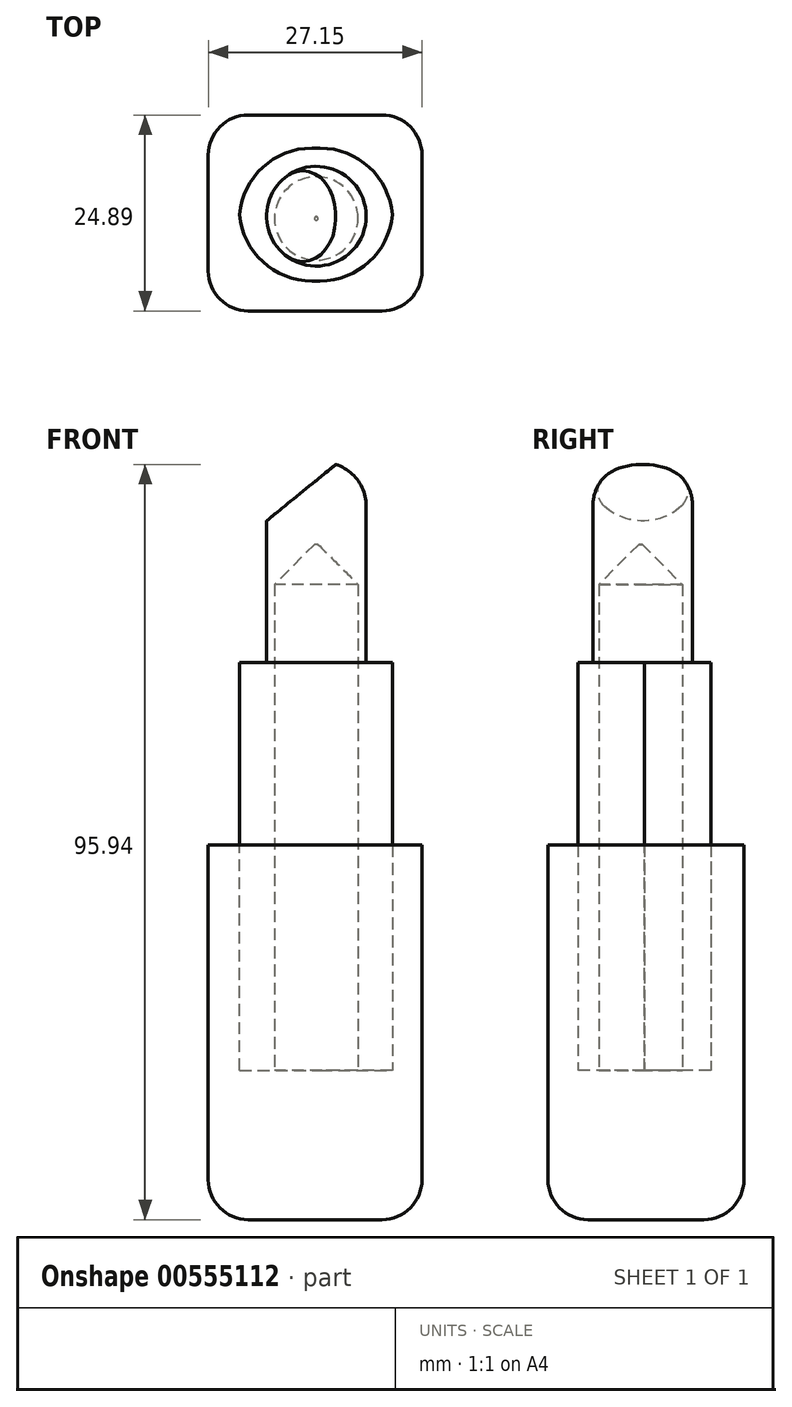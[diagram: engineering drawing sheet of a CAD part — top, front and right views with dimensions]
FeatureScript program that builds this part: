
annotation { "Feature Type Name" : "Feature", "Feature Type Description" : "" }
export const myFeature = defineFeature(function(context is Context, id is Id, definition is map)
    precondition{}
    {
        {
            var Q0;
            Q0=qCreatedBy(makeId("Front.planeOp"),FACE);
            var sketch = newSketch(context, id + "F0", { "sketchPlane" : qUnion([Q0])});
            skCircle(sketch, "E0", {"center": v(0, 0) * mm, "radius": 46.22 * mm});
            skSolve(sketch);
        }
        {
            var Q0;
            Q0=makeQuery(id+"F0.imprint","IMPRINT",FACE,{"disambiguationData":[TD([[makeQuery(id+"F0.imprint","IMPRINT",EDGE,{"derivedFrom":sQuery(id+"F0.wireOp",EDGE,"E0")}),1.0]])]});
            extrude(context, id + "F1", {"entities" : qUnion([Q0]), "depth" : 68.83 * mm, "offsetDistance" : 25.4 * mm});
        }
        {
            var Q0;
            Q0=makeQuery(id+"F1.opExtrude","SWEPT_FACE",FACE,{"disambiguationData":[OSD([sQuery(id+"F0.wireOp",EDGE,"E0")])]});
            fillet(context, id + "F2", {"entities" : qUnion([Q0]), "radius" : 33.73 * mm, "tangentPropagation" : true, "allowEdgeOverflow" : false});
        }
        {
            var Q0;
            Q0=makeQuery(id+"F1.opExtrude","SWEPT_BODY",BODY,{"disambiguationData":[OSD([sQuery(id+"F0.wireOp",EDGE,"E0")])]});
            deleteBodies(context, id + "F3", {"entities" : qUnion([Q0])});
        }
        {
            var Q0;
            Q0=qCreatedBy(makeId("Front.planeOp"),FACE);
            var sketch = newSketch(context, id + "F4", { "sketchPlane" : qUnion([Q0])});
            skLineSegment(sketch, "E1.bottom", {"start": v(-13.72, -18.98) * mm, "end": v(13.43, -18.98) * mm});
            skLineSegment(sketch, "E1.top", {"start": v(-13.72, 28.62) * mm, "end": v(13.43, 28.62) * mm});
            skLineSegment(sketch, "E1.left", {"start": v(-13.72, -18.98) * mm, "end": v(-13.72, 28.62) * mm});
            skLineSegment(sketch, "E1.right", {"start": v(13.43, -18.98) * mm, "end": v(13.43, 28.62) * mm});
            skSolve(sketch);
        }
        {
            var Q0;
            Q0=makeQuery(id+"F4.imprint","IMPRINT",FACE,{"disambiguationData":[TD([[makeQuery(id+"F4.imprint","IMPRINT",EDGE,{"derivedFrom":sQuery(id+"F4.wireOp",EDGE,"E1.bottom")}),1.0]])]});
            extrude(context, id + "F5", {"entities" : qUnion([Q0]), "depth" : 24.9 * mm, "offsetDistance" : 25.4 * mm});
        }
        {
            var Q0;
            Q0=makeQuery(id+"F5.opExtrude","CAP_EDGE",EDGE,{"disambiguationData":[OSD([sQuery(id+"F4.wireOp",EDGE,"E1.right")])],"isStart":false});
            var Q1;
            Q1=makeQuery(id+"F5.opExtrude","CAP_EDGE",EDGE,{"disambiguationData":[OSD([sQuery(id+"F4.wireOp",EDGE,"E1.right")])],"isStart":true});
            var Q2;
            Q2=makeQuery(id+"F5.opExtrude","CAP_EDGE",EDGE,{"disambiguationData":[OSD([sQuery(id+"F4.wireOp",EDGE,"E1.left")])],"isStart":true});
            var Q3;
            Q3=makeQuery(id+"F5.opExtrude","CAP_EDGE",EDGE,{"disambiguationData":[OSD([sQuery(id+"F4.wireOp",EDGE,"E1.left")])],"isStart":false});
            fillet(context, id + "F6", {"entities" : qUnion([Q0, Q1, Q2, Q3]), "radius" : 5.08 * mm, "tangentPropagation" : true, "allowEdgeOverflow" : false});
        }
        {
            var Q0;
            Q0=makeQuery(id+"F6.opFillet","BLEND_EDGE",EDGE,{"blendedFrom":[makeQuery(id+"F5.opExtrude","CAP_EDGE",EDGE,{"disambiguationData":[OSD([sQuery(id+"F4.wireOp",EDGE,"E1.left")])],"isStart":false}),makeQuery(id+"F5.opExtrude","SWEPT_FACE",FACE,{"disambiguationData":[OSD([sQuery(id+"F4.wireOp",EDGE,"E1.bottom")])]})],"blendedInto":[makeQuery(id+"F5.opExtrude","SWEPT_FACE",FACE,{"disambiguationData":[OSD([sQuery(id+"F4.wireOp",EDGE,"E1.bottom")])]})]});
            fillet(context, id + "F7", {"entities" : qUnion([Q0]), "radius" : 5.08 * mm, "tangentPropagation" : true, "allowEdgeOverflow" : false});
        }
        {
            var Q0;
            Q0=qCreatedBy(makeId("Top.planeOp"),FACE);
            var sketch = newSketch(context, id + "F8", { "sketchPlane" : qUnion([Q0])});
            skLineSegment(sketch, "E2.bottom", {"start": v(-9.77, -4.2) * mm, "end": v(9.69, -4.2) * mm});
            skLineSegment(sketch, "E2.top", {"start": v(-9.77, -21.07) * mm, "end": v(9.69, -21.07) * mm});
            skLineSegment(sketch, "E2.left", {"start": v(-9.77, -4.2) * mm, "end": v(-9.77, -21.07) * mm});
            skLineSegment(sketch, "E2.right", {"start": v(9.69, -4.2) * mm, "end": v(9.69, -21.07) * mm});
            skSolve(sketch);
        }
        {
            var Q0;
            Q0=makeQuery(id+"F8.imprint","IMPRINT",FACE,{"disambiguationData":[TD([[makeQuery(id+"F8.imprint","IMPRINT",EDGE,{"derivedFrom":sQuery(id+"F8.wireOp",EDGE,"E2.bottom")}),-1.0]])]});
            extrude(context, id + "F9", {"entities" : qUnion([Q0]), "depth" : 51.82 * mm, "offsetDistance" : 25.4 * mm});
        }
        {
            var Q0;
            Q0=makeQuery(id+"F9.opExtrude","SWEPT_EDGE",EDGE,{"disambiguationData":[OSD([sQuery(id+"F8.wireOp",EDGE,"E2.bottom"),sQuery(id+"F8.wireOp",EDGE,"E2.right")])]});
            var Q1;
            Q1=makeQuery(id+"F9.opExtrude","SWEPT_EDGE",EDGE,{"disambiguationData":[OSD([sQuery(id+"F8.wireOp",EDGE,"E2.top"),sQuery(id+"F8.wireOp",EDGE,"E2.right")])]});
            var Q2;
            Q2=makeQuery(id+"F9.opExtrude","SWEPT_EDGE",EDGE,{"disambiguationData":[OSD([sQuery(id+"F8.wireOp",EDGE,"E2.bottom"),sQuery(id+"F8.wireOp",EDGE,"E2.left")])]});
            var Q3;
            Q3=makeQuery(id+"F9.opExtrude","SWEPT_EDGE",EDGE,{"disambiguationData":[OSD([sQuery(id+"F8.wireOp",EDGE,"E2.top"),sQuery(id+"F8.wireOp",EDGE,"E2.left")])]});
            fillet(context, id + "F10", {"entities" : qUnion([Q0, Q1, Q2, Q3]), "radius" : 9.2 * mm, "tangentPropagation" : true, "allowEdgeOverflow" : false});
        }
        {
            var Q0;
            Q0=qCreatedBy(makeId("Top.planeOp"),FACE);
            var sketch = newSketch(context, id + "F11", { "sketchPlane" : qUnion([Q0])});
            skCircle(sketch, "E3", {"center": v(0, -13.14) * mm, "radius": 5.3 * mm});
            skSolve(sketch);
        }
        {
            var Q0;
            Q0 = qSketchRegion(id + "F11", true);
            extrude(context, id + "F12", {"entities" : qUnion([Q0]), "depth" : 66.8 * mm, "offsetDistance" : 25.4 * mm});
        }
        {
            var Q0;
            Q0=makeQuery(id+"F12.opExtrude","CAP_EDGE",EDGE,{"disambiguationData":[OSD([sQuery(id+"F11.wireOp",EDGE,"E3")])],"isStart":false});
            chamfer(context, id + "F13", {"entities" : qUnion([Q0]), "width" : 5.08 * mm, "tangentPropagation" : true});
        }
        {
            var Q0;
            Q0=makeQuery(id+"F9.opExtrude","CAP_FACE",FACE,{"disambiguationData":[OSD([sQuery(id+"F8.wireOp",EDGE,"E2.bottom"),sQuery(id+"F8.wireOp",EDGE,"E2.top"),sQuery(id+"F8.wireOp",EDGE,"E2.left"),sQuery(id+"F8.wireOp",EDGE,"E2.right")])],"isStart":false});
            var sketch = newSketch(context, id + "F14", { "sketchPlane" : qUnion([Q0])});
            skCircle(sketch, "E4", {"center": v(0, -12.85) * mm, "radius": 6.33 * mm});
            skSolve(sketch);
        }
        {
            var Q0;
            Q0=makeQuery(id+"F14.imprint","IMPRINT",FACE,{"disambiguationData":[TD([[makeQuery(id+"F14.imprint","IMPRINT",EDGE,{"derivedFrom":sQuery(id+"F14.wireOp",EDGE,"E4")}),1.0]])]});
            extrude(context, id + "F15", {"entities" : qUnion([Q0]), "depth" : 25.4 * mm, "offsetDistance" : 25.4 * mm});
        }
        {
            var Q0;
            Q0=makeQuery(id+"F15.opExtrude","CAP_EDGE",EDGE,{"disambiguationData":[OSD([sQuery(id+"F14.wireOp",EDGE,"E4")])],"isStart":false});
            fillet(context, id + "F16", {"entities" : qUnion([Q0]), "radius" : 5.52 * mm, "tangentPropagation" : true, "allowEdgeOverflow" : false});
        }
        {
            var Q0;
            Q0=qCreatedBy(makeId("Front.planeOp"),FACE);
            var sketch = newSketch(context, id + "F17", { "sketchPlane" : qUnion([Q0])});
            skLineSegment(sketch, "E5", {"start": v(-9.31, 67.36) * mm, "end": v(7.76, 81.25) * mm});
            skLineSegment(sketch, "E6", {"start": v(7.76, 81.25) * mm, "end": v(-14.3, 84.54) * mm});
            skLineSegment(sketch, "E7", {"start": v(-14.3, 84.54) * mm, "end": v(-9.31, 67.36) * mm});
            skSolve(sketch);
        }
        {
            var Q0;
            Q0=makeQuery(id+"F17.imprint","IMPRINT",FACE,{"disambiguationData":[TD([[makeQuery(id+"F17.imprint","IMPRINT",EDGE,{"derivedFrom":sQuery(id+"F17.wireOp",EDGE,"E5")}),1.0]])]});
            extrude(context, id + "F18", {"entities" : qUnion([Q0]), "operationType" : NewBodyOperationType.REMOVE, "depth" : 26.42 * mm, "offsetDistance" : 25.4 * mm});
        }
    });
